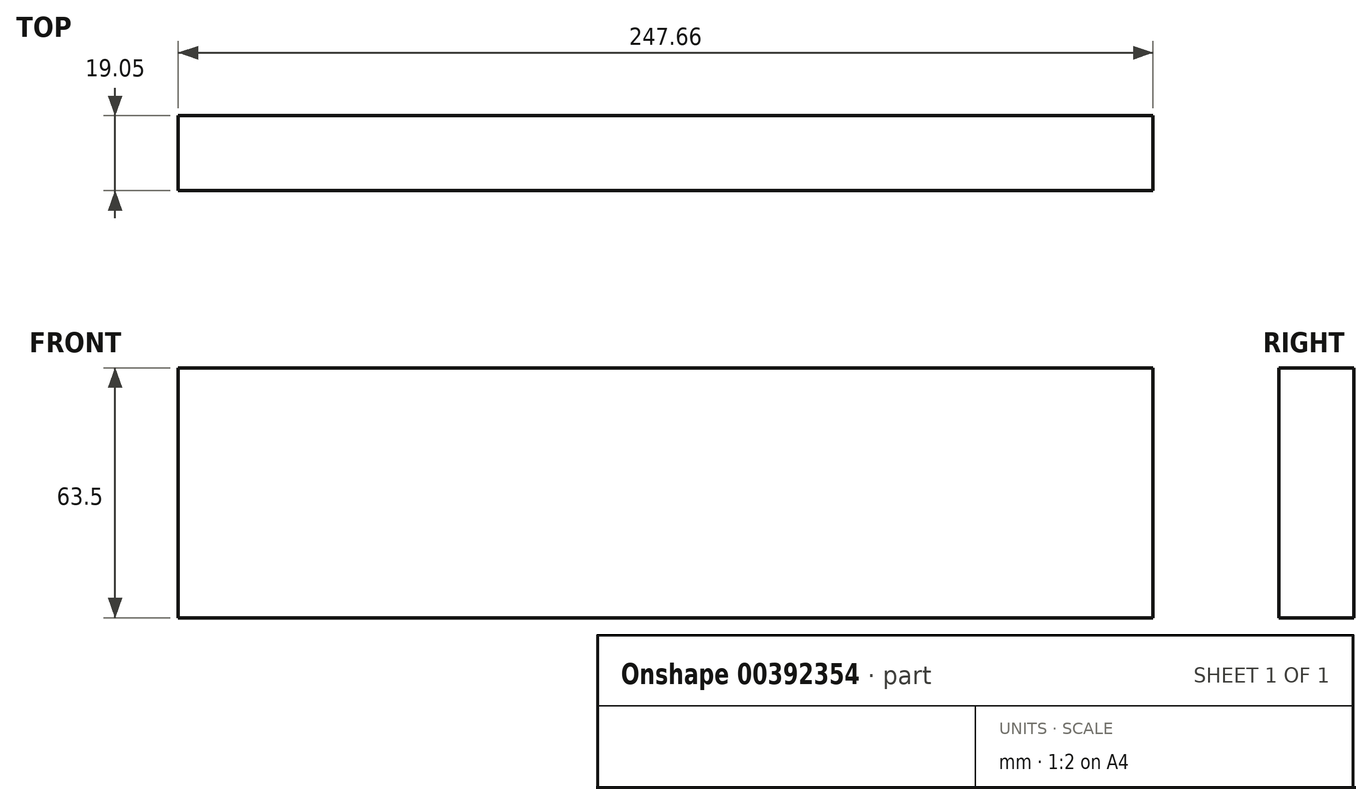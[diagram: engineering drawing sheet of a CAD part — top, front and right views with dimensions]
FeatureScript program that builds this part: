
annotation { "Feature Type Name" : "Feature", "Feature Type Description" : "" }
export const myFeature = defineFeature(function(context is Context, id is Id, definition is map)
    precondition{}
    {
        {
            var Q0;
            Q0=qCreatedBy(makeId("Front.planeOp"),FACE);
            var sketch = newSketch(context, id + "F0", { "sketchPlane" : qUnion([Q0])});
            skLineSegment(sketch, "E0.bottom", {"start": v(-123.83, 0) * mm, "end": v(123.83, 0) * mm});
            skLineSegment(sketch, "E0.top", {"start": v(-123.83, -63.5) * mm, "end": v(123.83, -63.5) * mm});
            skLineSegment(sketch, "E0.left", {"start": v(-123.83, 0) * mm, "end": v(-123.83, -63.5) * mm});
            skLineSegment(sketch, "E0.right", {"start": v(123.83, 0) * mm, "end": v(123.83, -63.5) * mm});
            skSolve(sketch);
        }
        {
            var Q0;
            Q0=makeQuery(id+"F0.imprint","IMPRINT",FACE,{"disambiguationData":[TD([[makeQuery(id+"F0.imprint","IMPRINT",EDGE,{"derivedFrom":sQuery(id+"F0.wireOp",EDGE,"E0.bottom")}),-1.0]])]});
            extrude(context, id + "F1", {"entities" : qUnion([Q0]), "depth" : 19.05 * mm});
        }
    });
